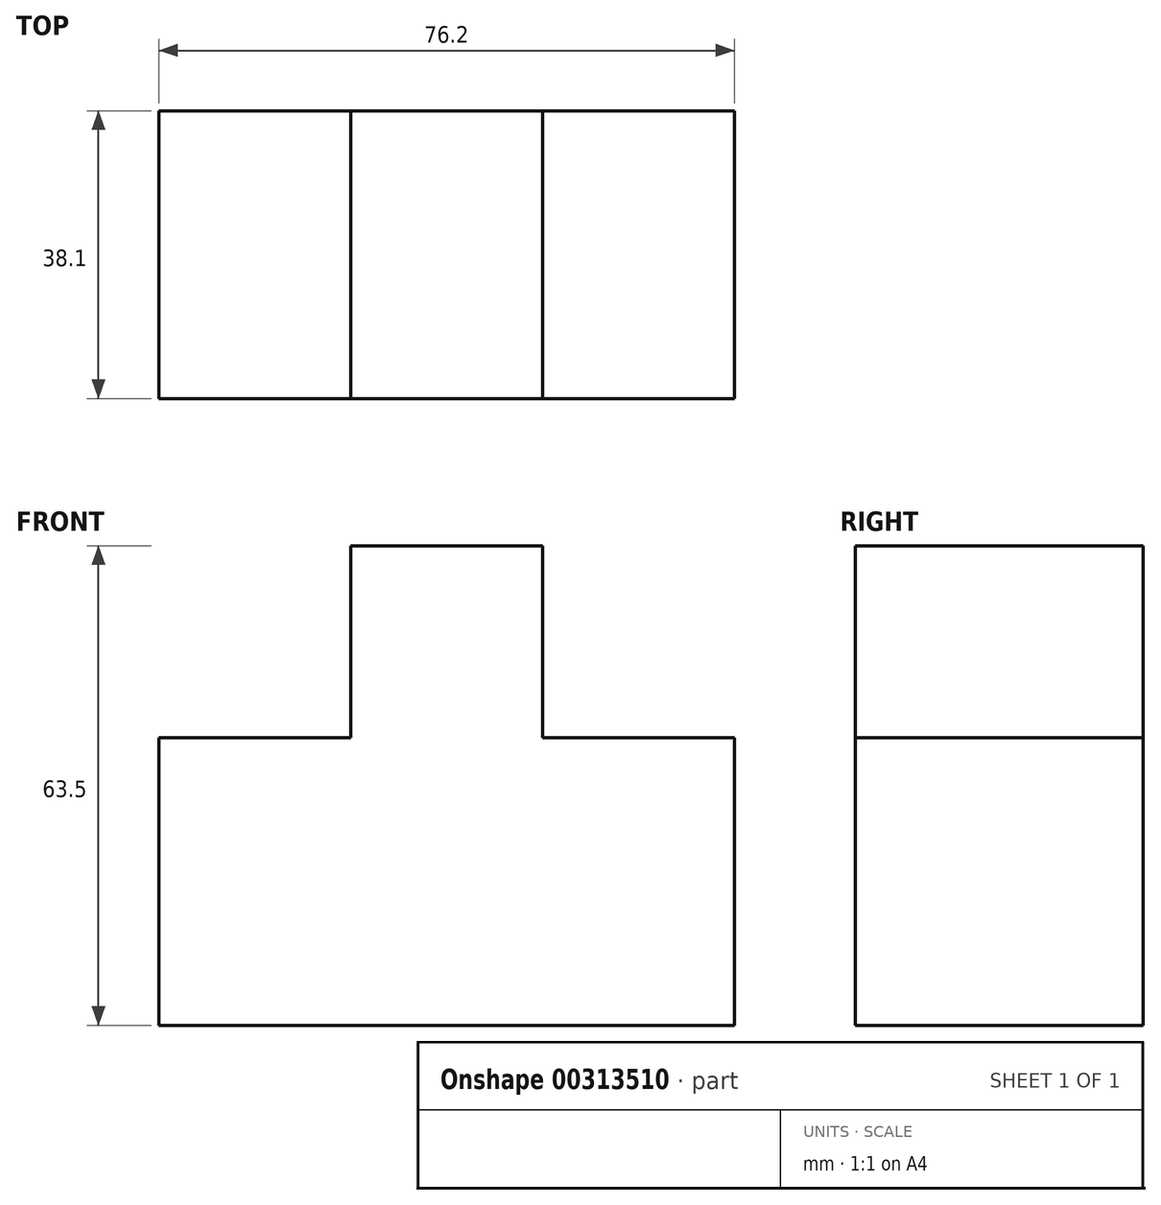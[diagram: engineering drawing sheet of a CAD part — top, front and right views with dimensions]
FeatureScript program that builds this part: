
annotation { "Feature Type Name" : "Feature", "Feature Type Description" : "" }
export const myFeature = defineFeature(function(context is Context, id is Id, definition is map)
    precondition{}
    {
        {
            var Q0;
            Q0=qCreatedBy(makeId("Front.planeOp"),FACE);
            var sketch = newSketch(context, id + "F0", { "sketchPlane" : qUnion([Q0])});
            skLineSegment(sketch, "E0", {"start": v(-43.92, -44.56) * mm, "end": v(44.98, -44.56) * mm});
            skLineSegment(sketch, "E1", {"start": v(44.98, -44.56) * mm, "end": v(44.98, -6.46) * mm});
            skLineSegment(sketch, "E2", {"start": v(44.98, -6.46) * mm, "end": v(19.58, -6.46) * mm});
            skLineSegment(sketch, "E3", {"start": v(19.58, -6.46) * mm, "end": v(19.58, 18.94) * mm});
            skLineSegment(sketch, "E4", {"start": v(19.58, 18.94) * mm, "end": v(-5.82, 18.94) * mm});
            skLineSegment(sketch, "E5", {"start": v(-5.82, 18.94) * mm, "end": v(-5.82, -6.46) * mm});
            skLineSegment(sketch, "E6", {"start": v(-5.82, -6.46) * mm, "end": v(-31.22, -6.46) * mm});
            skLineSegment(sketch, "E7", {"start": v(-31.22, -6.46) * mm, "end": v(-31.22, -44.56) * mm});
            skSolve(sketch);
        }
        {
            var Q0;
            {var subQ0=sQuery(id+"F0.wireOp",EDGE,"E1");Q0=makeQuery(id+"F0.imprint","IMPRINT",FACE,{"disambiguationData":[TD([[makeQuery(id+"F0.imprint","IMPRINT",EDGE,{"derivedFrom":subQ0}),1.0]])]});}
            extrude(context, id + "F1", {"entities" : qUnion([Q0]), "depth" : 38.1 * mm});
        }
    });
